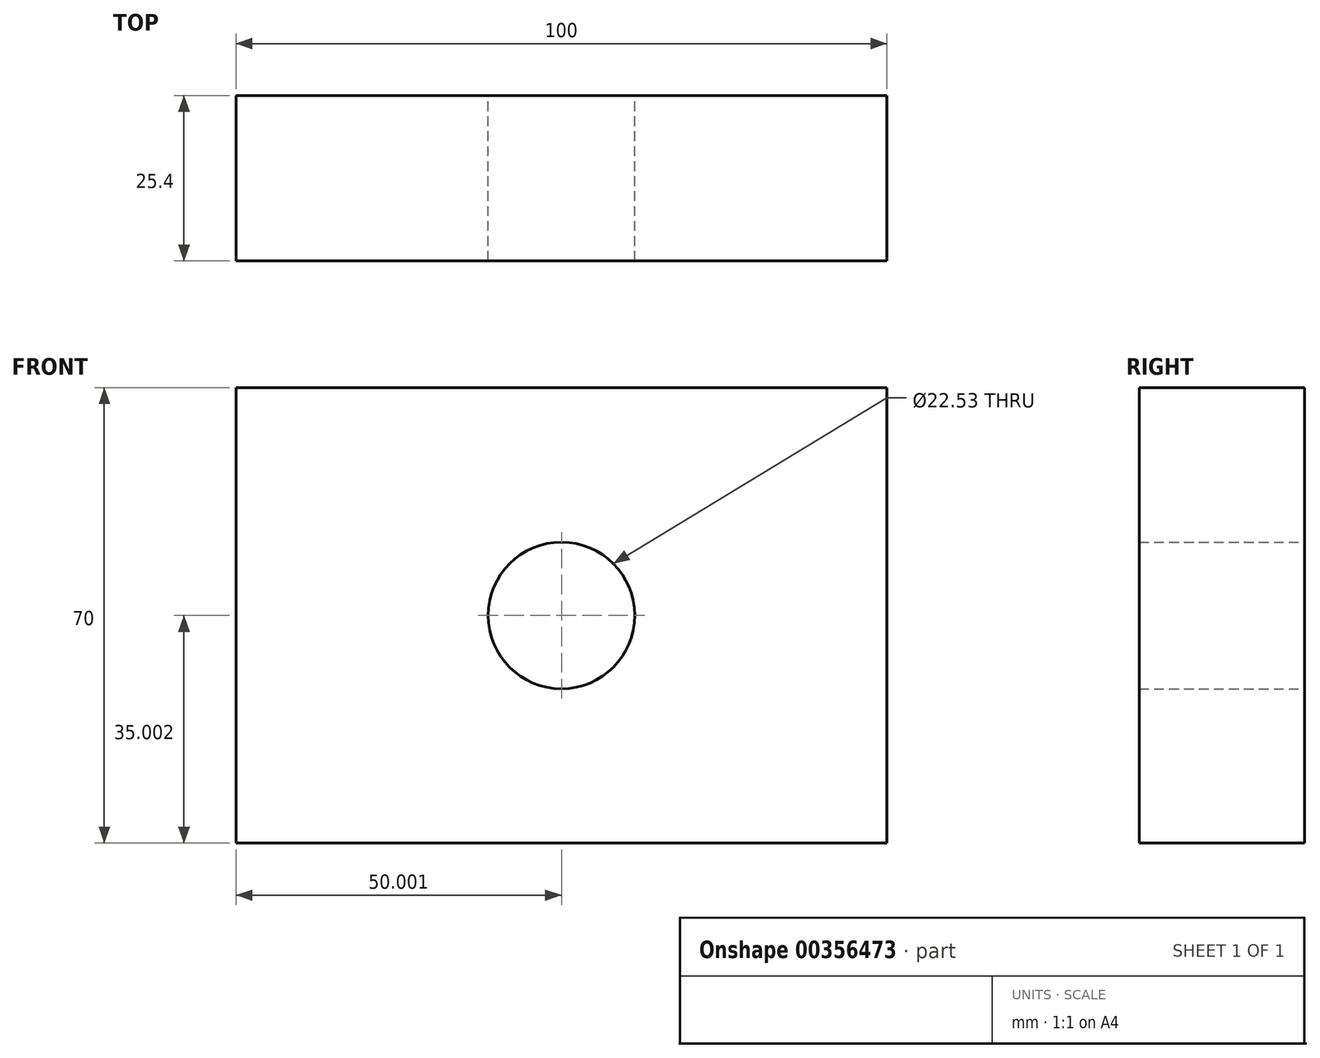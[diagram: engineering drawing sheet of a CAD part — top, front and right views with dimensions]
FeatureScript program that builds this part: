
annotation { "Feature Type Name" : "Feature", "Feature Type Description" : "" }
export const myFeature = defineFeature(function(context is Context, id is Id, definition is map)
    precondition{}
    {
        {
            var Q0;
            Q0=qCreatedBy(makeId("Front.planeOp"),FACE);
            var sketch = newSketch(context, id + "F0", { "sketchPlane" : qUnion([Q0])});
            skLineSegment(sketch, "E0.bottom", {"start": v(-51.27, 20.11) * mm, "end": v(48.73, 20.11) * mm});
            skLineSegment(sketch, "E0.top", {"start": v(-51.27, -49.89) * mm, "end": v(48.73, -49.89) * mm});
            skLineSegment(sketch, "E0.left", {"start": v(-51.27, 20.11) * mm, "end": v(-51.27, -49.89) * mm});
            skLineSegment(sketch, "E0.right", {"start": v(48.73, 20.11) * mm, "end": v(48.73, -49.89) * mm});
            skCircle(sketch, "E1", {"center": v(-1.27, -14.89) * mm, "radius": 11.27 * mm});
            skPoint(sketch, "E1.centerSnap0", {"position": v(-1.27, 20.11) * mm});
            skPoint(sketch, "E1.centerSnap1", {"position": v(-51.27, -14.89) * mm});
            skSolve(sketch);
        }
        {
            var Q0;
            Q0 = qSketchRegion(id + "F0", true);
            extrude(context, id + "F1", {"entities" : qUnion([Q0]), "depth" : 25.4 * mm});
        }
    });
